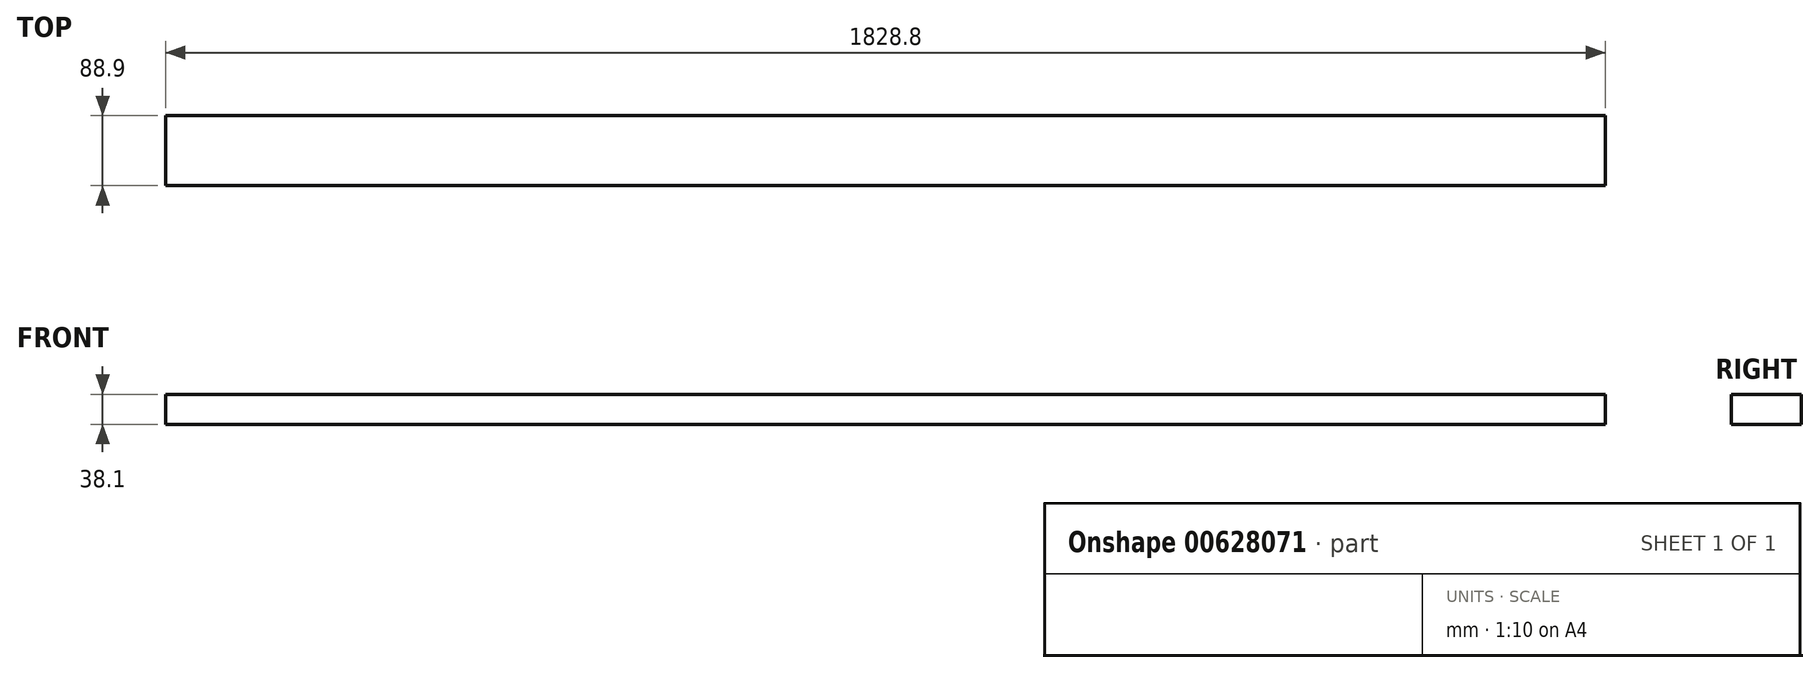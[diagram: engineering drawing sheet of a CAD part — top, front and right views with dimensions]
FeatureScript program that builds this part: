
annotation { "Feature Type Name" : "Feature", "Feature Type Description" : "" }
export const myFeature = defineFeature(function(context is Context, id is Id, definition is map)
    precondition{}
    {
        {
            var Q0;
            Q0=qCreatedBy(makeId("Top.planeOp"),FACE);
            var sketch = newSketch(context, id + "F0", { "sketchPlane" : qUnion([Q0])});
            skLineSegment(sketch, "E0.bottom", {"start": v(-443.47, 60.85) * mm, "end": v(1385.33, 60.85) * mm});
            skLineSegment(sketch, "E0.top", {"start": v(-443.47, -28.05) * mm, "end": v(1385.33, -28.05) * mm});
            skLineSegment(sketch, "E0.left", {"start": v(-443.47, 60.85) * mm, "end": v(-443.47, -28.05) * mm});
            skLineSegment(sketch, "E0.right", {"start": v(1385.33, 60.85) * mm, "end": v(1385.33, -28.05) * mm});
            skSolve(sketch);
        }
        {
            var Q0;
            Q0=makeQuery(id+"F0.imprint","IMPRINT",FACE,{"disambiguationData":[TD([[makeQuery(id+"F0.imprint","IMPRINT",EDGE,{"derivedFrom":sQuery(id+"F0.wireOp",EDGE,"E0.bottom")}),-1.0]])]});
            extrude(context, id + "F1", {"entities" : qUnion([Q0]), "depth" : 38.1 * mm, "offsetDistance" : 25.4 * mm});
        }
    });
